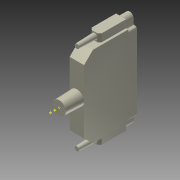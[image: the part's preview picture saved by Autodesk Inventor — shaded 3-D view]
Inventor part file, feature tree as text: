
AUTODESK INVENTOR PART (.ipt)
format: ipt  version: 2013 (Build 170138000, 138)  size: 214,528 bytes
history: native  units: in
note: dims shown in document units (in); Inventor stores cm internally (conversion verified against a paired STEP export)
features: extrude x6, sketch x6, other x4, draft x3, chamfer x2, plane x2, projected_geometry x1
ambient origin geometry x8: Origin, YZ Plane, XZ Plane, XY Plane, X Axis, Y Axis, Z Axis, Center Point
bodies: Solid1 (feature_tree)
feature tree (24):
  extrude  "Extrusion1"  Depth=1.0in TaperAngle=0.0deg
  sketch  "Sketch2"  dims[d6=0.75in d7=0.0in d8=0.0625in d9=0.125in d10=45.0deg]
  extrude  "Extrusion3"  Depth=0.0625in TaperAngle=45.0deg
  extrude  "Extrusion4"  Depth=0.25in TaperAngle=45.0deg
  chamfer  "Chamfer1"  Distance=0.5in
  extrude  "Extrusion5"  Depth=0.125in
  chamfer  "Chamfer2"  Distance=0.5in
  extrude  "Extrusion6"  Depth=0.0137in
  draft  "FaceDraft1"
  extrude  "Extrusion7"  Depth=0.0137in
  draft  "FaceDraft2"
  draft  "FaceDraft3"
  sketch  "Sketch6"  dims[d21=0.125in d22=0.5in d23=0.0in d24=0.0137in d25=0.0137in d26=0.125in d27=0.25in]
  other  "Work Point2"
  other  "Work Point3"
  sketch  "Sketch1"  dims[d0=0.243in d1=0.0in d4=1.0in d5=0.0in]
  sketch  "Sketch3"  dims[d11=0.25in d12=0.0in d13=0.25in d14=0.125in d15=45.0deg]
  sketch  "Sketch4"  dims[d16=0.375in d17=0.5in d18=0.0in]
  sketch  "Sketch5"  dims[d19=0.0137in d20=0.125in]
  projected_geometry  "Projected Loop1"
  plane  "Work Plane1"
  other  "Work Axis1"
  plane  "Work Plane2"
  other  "Work Axis2"
